# Revit family: Door-Sliding-All_Weather-Series_8100-Pocket
name_source: partatom
category: Doors
units: mm (PartAtom-declared; Revit-internal decimal feet)

## family parameters
Always vertical = Yes
Classification Number = 23.30.10.00
Cut with Voids When Loaded = No
Host = Wall
Room Calculation Point = No
Shared = No

## types (3) — shared parameters
Analytic Construction = <None>
Assembly Code = B2030110
Exterior Trim = No
Exterior Trim Finish = Metal-Aluminum-All_Weather-Standard-White
Finish = Metal-Aluminum-All_Weather-Standard-White
Frame Projection Ext. = 0' - 1"
Frame Width = 0' - 3"
Function = Exterior
Glazing = Glass-All_Weather-OA-Insulated_Glass
Height = 8' - 0"
Inset = 0' - 0"
Interior Trim = No
Interior Trim Finish = Metal-Aluminum-All_Weather-Standard-White
Jamb Ext Finish = Metal-Aluminum-All_Weather-Standard-White
Manufacturer = All Weather Architectural Aluminum
Max Panel Height = 12' - 1 1/4"
Max Panel Width = 6' - 0"
Min Panel Width = 1' - 8 1/2"
Model = Thermally Broken Pocket Door
Offset = 0' - 0"
Opening Width = 8' - 0"
Operation = Sliding
Panel Height = 7' - 10 3/4"
Panel Thickness = 0' - 2"
Product Documentation Link = https://www.allweatheraa.com
Product Name = Series 8100
Product Page URL = https://www.allweatheraa.com
Requested Height = 8' - 0"
Requested Opening Width = 8' - 0"
Rough Height = 8' - 0 1/2"
Type Comments = Multi-Panel Sliding Door
URL = https://www.allweatheraa.com
Wall Closure = By host

## per-type parameters (varying)
| type | 2 Track | 3 Track | 4 Track | Center Panel Location | Description | End Panel Offset | Frame Projection Int. | Jamb Extensions | Max Width | Min Width | Not 2 Track | Number of Panels | Panel Offset | Panel Spacing | Panel Width | Panel Width End Panel | Pocket Width | Rough Width | Thickness | Width |
| Pocket Door - XXXP | No | Yes | No | 0' - 0" | XXXP | 0' - 5" | 0' - 5 1/2" | No | 18' - 1 5/8" | 5' - 3 1/8" | Yes | 3 | 0' - 4 15/16" | 0' - 2 1/2" | 2' - 10 5/32" | 2' - 11 3/4" | 3' - 0 5/32" | 11' - 3 5/32" | 0' - 6" | 11' - 2 5/32" |
| Pocket Door - XXXXP | No | No | Yes | 0' - 11 13/16" | XXXXP | 0' - 7" | 0' - 5 1/2" | No | 24' - 1 5/8" | 6' - 11 5/8" | Yes | 4 | 0' - 2 31/32" | 0' - 2" | 2' - 2 9/32" | 2' - 3 27/32" | 2' - 4 9/32" | 10' - 7 9/32" | 0' - 8" | 10' - 6 9/32" |
| Pocket Door - XXP | Yes | No | No | 1' - 11 21/32" | XXP | 0' - 3" | 0' - 1" | Yes | 12' - 1 5/8" | 3' - 6 5/8" | No | 2 | 0' - 2 31/32" | 0' - 2" | 4' - 1 15/16" | 4' - 3 17/32" | 4' - 3 15/16" | 12' - 6 15/16" | 0' - 4" | 12' - 5 15/16" |

## geometry (parser evidence)
native form markers: Sweep x11
no freeform markers — native parametric forms only
